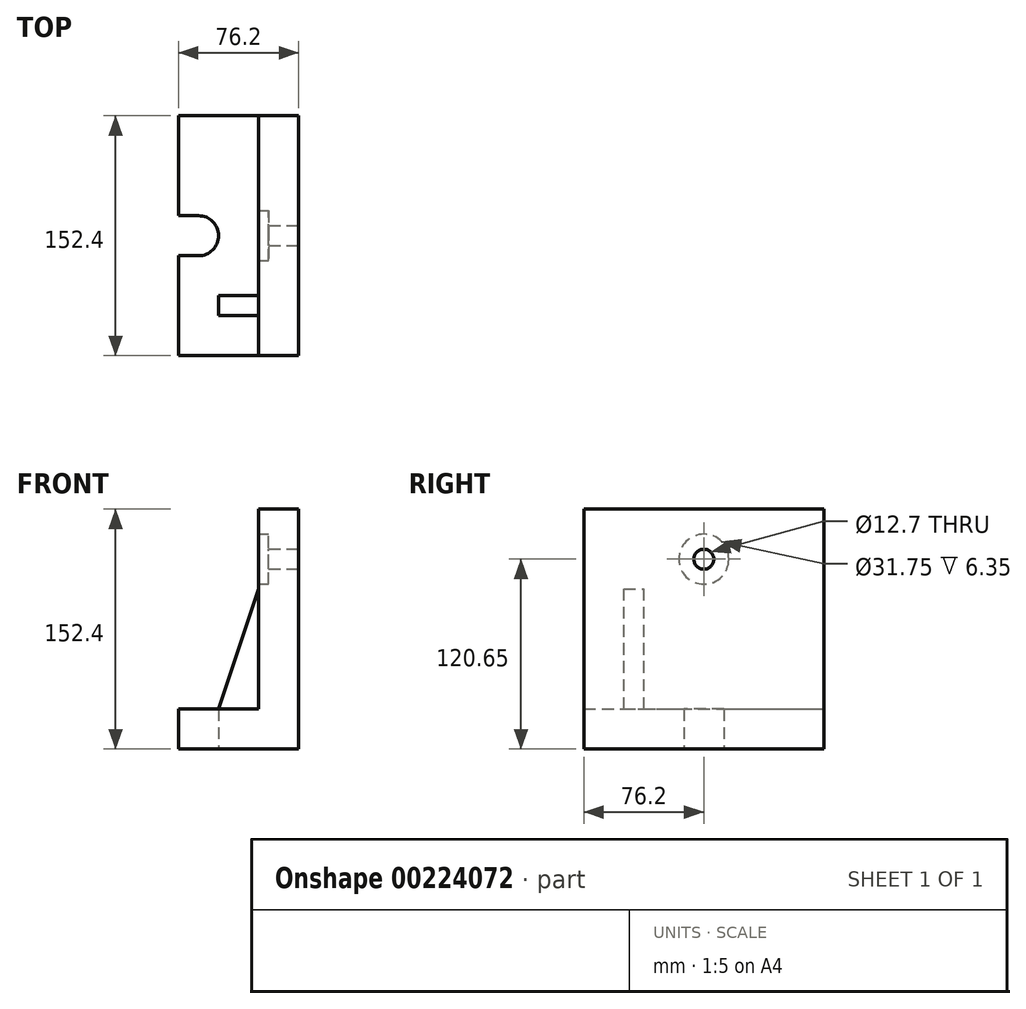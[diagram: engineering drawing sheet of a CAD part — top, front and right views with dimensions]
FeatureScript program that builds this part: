
annotation { "Feature Type Name" : "Feature", "Feature Type Description" : "" }
export const myFeature = defineFeature(function(context is Context, id is Id, definition is map)
    precondition{}
    {
        {
            var Q0;
            Q0=qCreatedBy(makeId("Front.planeOp"),FACE);
            var sketch = newSketch(context, id + "F0", { "sketchPlane" : qUnion([Q0])});
            skLineSegment(sketch, "E0", {"start": v(0, 0) * mm, "end": v(0, 152.4) * mm});
            skLineSegment(sketch, "E1", {"start": v(0, 152.4) * mm, "end": v(-25.4, 152.4) * mm});
            skLineSegment(sketch, "E2", {"start": v(-25.4, 152.4) * mm, "end": v(-25.4, 25.4) * mm});
            skLineSegment(sketch, "E3", {"start": v(-25.4, 25.4) * mm, "end": v(-76.2, 25.4) * mm});
            skLineSegment(sketch, "E4", {"start": v(-76.2, 25.4) * mm, "end": v(-76.2, 0) * mm});
            skLineSegment(sketch, "E5", {"start": v(-76.2, 0) * mm, "end": v(0, 0) * mm});
            skSolve(sketch);
        }
        {
            var Q0;
            Q0 = qSketchRegion(id + "F0", true);
            extrude(context, id + "F1", {"entities" : qUnion([Q0]), "endBound" : BoundingType.SYMMETRIC, "depth" : 152.4 * mm});
        }
        {
            var Q0;
            Q0=qCreatedBy(makeId("Right.planeOp"),FACE);
            var sketch = newSketch(context, id + "F2", { "sketchPlane" : qUnion([Q0])});
            skLineSegment(sketch, "E6", {"start": v(0, 0) * mm, "end": v(0, 120.65) * mm});
            skCircle(sketch, "E7", {"center": v(0, 120.65) * mm, "radius": 6.35 * mm});
            skSolve(sketch);
        }
        {
            var Q0;
            Q0=makeQuery(id+"F2.imprint","IMPRINT",FACE,{"disambiguationData":[TD([[makeQuery(id+"F2.imprint","IMPRINT",EDGE,{"derivedFrom":sQuery(id+"F2.wireOp",EDGE,"E7")}),1.0]])]});
            var Q1;
            Q1=sQuery(id+"F2.wireOp",EDGE,"E7");
            extrude(context, id + "F3", {"entities" : qUnion([Q0]), "operationType" : NewBodyOperationType.REMOVE, "surfaceEntities" : qUnion([Q1]), "oppositeDirection" : true, "depth" : 25.4 * mm, "hasSecondDirection" : true, "secondDirectionOppositeDirection" : false, "secondDirectionDepth" : 25.4 * mm});
        }
        {
            var Q0;
            Q0=qCreatedBy(makeId("Right.planeOp"),FACE);
            var sketch = newSketch(context, id + "F4", { "sketchPlane" : qUnion([Q0])});
            skCircle(sketch, "E8", {"center": v(0, 120.65) * mm, "radius": 15.88 * mm});
            skSolve(sketch);
        }
        {
            var Q0;
            Q0 = qSketchRegion(id + "F4", true);
            var Q1;
            Q1=sQuery(id+"F4.wireOp",EDGE,"E8");
            extrude(context, id + "F5", {"entities" : qUnion([Q0]), "operationType" : NewBodyOperationType.REMOVE, "surfaceEntities" : qUnion([Q1]), "oppositeDirection" : true, "depth" : 34.54 * mm, "hasSecondDirection" : true, "secondDirectionOppositeDirection" : true, "secondDirectionDepth" : 19.05 * mm});
        }
        {
            var Q0;
            Q0=qCreatedBy(makeId("Top.planeOp"),FACE);
            var sketch = newSketch(context, id + "F6", { "sketchPlane" : qUnion([Q0])});
            skLineSegment(sketch, "E9", {"start": v(-76.2, 0) * mm, "end": v(-76.2, 12.7) * mm});
            skLineSegment(sketch, "E10", {"start": v(-76.2, -12.7) * mm, "end": v(-76.2, 0) * mm});
            skLineSegment(sketch, "E11", {"start": v(-76.2, 12.7) * mm, "end": v(-63.5, 12.7) * mm});
            skLineSegment(sketch, "E12", {"start": v(-76.2, -12.7) * mm, "end": v(-63.5, -12.7) * mm});
            skArc(sketch, "E13", {"start": v(-63.5, -12.7) * mm, "mid": v(-50.8, 0) * mm, "end": v(-63.5, 12.7) * mm});
            skSolve(sketch);
        }
        {
            var Q0;
            Q0 = qSketchRegion(id + "F6", true);
            extrude(context, id + "F7", {"entities" : qUnion([Q0]), "operationType" : NewBodyOperationType.REMOVE, "endBound" : BoundingType.SYMMETRIC, "depth" : 51.82 * mm});
        }
        {
            var Q0;
            Q0=qCreatedBy(makeId("Front.planeOp"),FACE);
            cPlane(context, id + "F8", {"entities" : qUnion([Q0]), "cplaneType" : CPlaneType.OFFSET, "offset" : 44.45 * mm, "width" : 152.4 * mm, "height" : 152.4 * mm});
        }
        {
            var Q0;
            Q0=qCreatedBy(id+"F8.planeOp",FACE);
            var sketch = newSketch(context, id + "F9", { "sketchPlane" : qUnion([Q0])});
            skLineSegment(sketch, "E14", {"start": v(-25.4, 25.4) * mm, "end": v(-25.4, 101.6) * mm});
            skLineSegment(sketch, "E15", {"start": v(-25.4, 25.4) * mm, "end": v(-50.8, 25.4) * mm});
            skLineSegment(sketch, "E16", {"start": v(-25.4, 101.6) * mm, "end": v(-50.8, 25.4) * mm});
            skSolve(sketch);
        }
        {
            var Q0;
            Q0 = qSketchRegion(id + "F9", true);
            extrude(context, id + "F10", {"entities" : qUnion([Q0]), "operationType" : NewBodyOperationType.ADD, "endBound" : BoundingType.SYMMETRIC, "depth" : 12.7 * mm});
        }
    });
